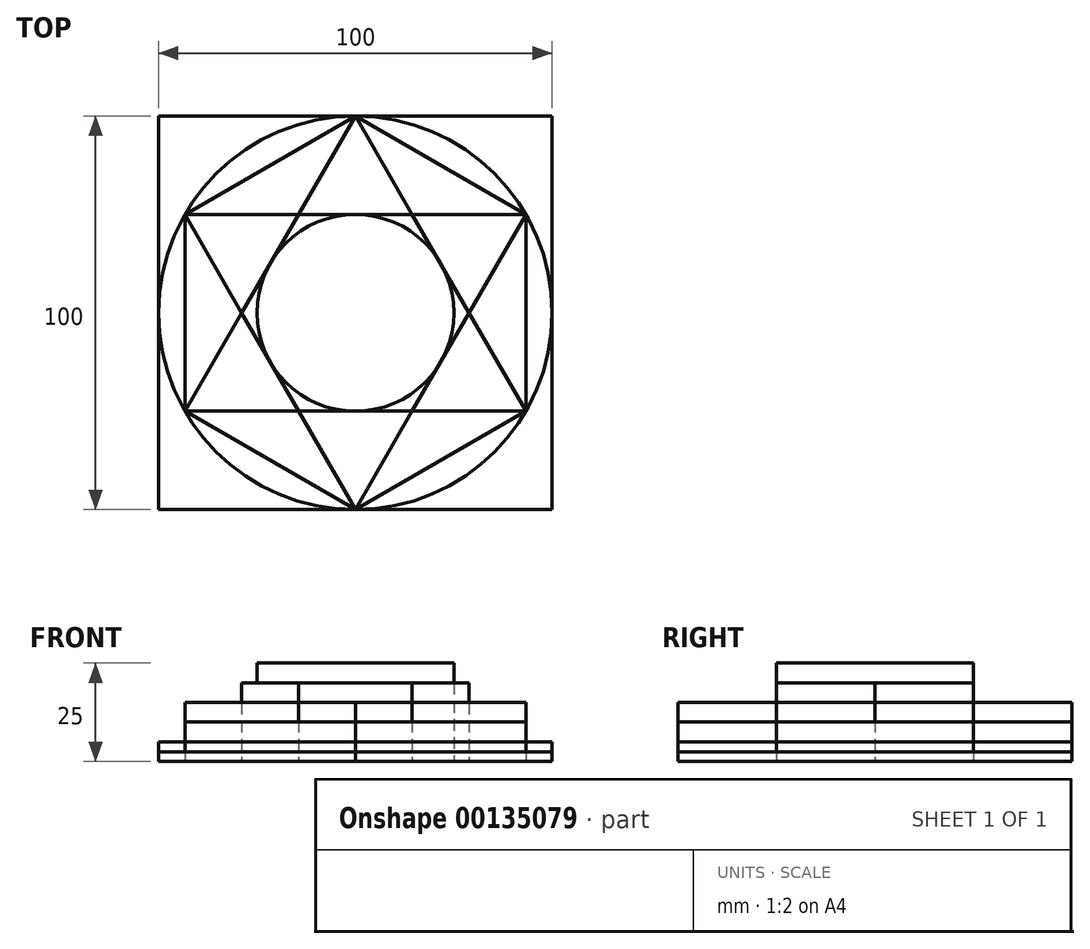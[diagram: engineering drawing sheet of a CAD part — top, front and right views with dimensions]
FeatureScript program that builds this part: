
annotation { "Feature Type Name" : "Feature", "Feature Type Description" : "" }
export const myFeature = defineFeature(function(context is Context, id is Id, definition is map)
    precondition{}
    {
        {
            var Q0;
            Q0=qCreatedBy(makeId("Top.planeOp"),FACE);
            var sketch = newSketch(context, id + "F0", { "sketchPlane" : qUnion([Q0])});
            skCircle(sketch, "E0", {"center": v(0, 0) * mm, "radius": 50 * mm});
            skCircle(sketch, "E1.cCircle", {"center": v(0, 0) * mm, "radius": 50 * mm, "construction": true});
            skLineSegment(sketch, "E1.0", {"start": v(0, 50) * mm, "end": v(43.3, 25) * mm});
            skLineSegment(sketch, "E1.1", {"start": v(43.3, 25) * mm, "end": v(43.3, -25) * mm});
            skLineSegment(sketch, "E1.2", {"start": v(43.3, -25) * mm, "end": v(0, -50) * mm});
            skLineSegment(sketch, "E1.3", {"start": v(0, -50) * mm, "end": v(-43.3, -25) * mm});
            skLineSegment(sketch, "E1.4", {"start": v(-43.3, -25) * mm, "end": v(-43.3, 25) * mm});
            skLineSegment(sketch, "E1.5", {"start": v(-43.3, 25) * mm, "end": v(0, 50) * mm});
            skLineSegment(sketch, "E2", {"start": v(0, 50) * mm, "end": v(-43.3, -25) * mm});
            skLineSegment(sketch, "E3", {"start": v(-43.3, -25) * mm, "end": v(43.3, -25) * mm});
            skLineSegment(sketch, "E4", {"start": v(-43.3, 25) * mm, "end": v(43.3, 25) * mm});
            skLineSegment(sketch, "E5", {"start": v(0, -50) * mm, "end": v(-43.3, 25) * mm});
            skLineSegment(sketch, "E6", {"start": v(0, 50) * mm, "end": v(43.3, -25) * mm});
            skLineSegment(sketch, "E7", {"start": v(43.3, 25) * mm, "end": v(0, -50) * mm});
            skCircle(sketch, "E8", {"center": v(0, 0) * mm, "radius": 25 * mm});
            skLineSegment(sketch, "E9.0", {"start": v(-50, 50) * mm, "end": v(50, 50) * mm});
            skLineSegment(sketch, "E9.1", {"start": v(50, 50) * mm, "end": v(50, -50) * mm});
            skLineSegment(sketch, "E9.2", {"start": v(50, -50) * mm, "end": v(-50, -50) * mm});
            skLineSegment(sketch, "E9.3", {"start": v(-50, -50) * mm, "end": v(-50, 50) * mm});
            skPoint(sketch, "E9.0.midPoint", {"position": v(0, 50) * mm});
            skSolve(sketch);
        }
        {
            var Q0;
            {var subQ0=sQuery(id+"F0.wireOp",EDGE,"E8");var subQ4=makeQuery(id+"F0.imprint","INTERSECT",VERTEX,{"derivedFrom":[sQuery(id+"F0.wireOp",EDGE,"E4"),subQ0]});Q0=makeQuery(id+"F0.imprint","IMPRINT",FACE,{"disambiguationData":[TD([[makeQuery(id+"F0.imprint","IMPRINT",EDGE,{"disambiguationData":[TD([[subQ4,1.0]])],"derivedFrom":subQ0}),1.0]])]});}
            extrude(context, id + "F1", {"entities" : qUnion([Q0]), "depth" : 25 * mm});
        }
        {
            var Q0;
            {var subQ0=sQuery(id+"F0.wireOp",EDGE,"E8");var subQ1=sQuery(id+"F0.wireOp",EDGE,"E2");var subQ2=makeQuery(id+"F0.imprint","INTERSECT",VERTEX,{"derivedFrom":[subQ1,subQ0]});Q0=makeQuery(id+"F0.imprint","IMPRINT",FACE,{"disambiguationData":[TD([[makeQuery(id+"F0.imprint","IMPRINT",EDGE,{"disambiguationData":[TD([[subQ2,-1.0]])],"derivedFrom":subQ1}),1.0]])]});}
            var Q1;
            {var subQ0=sQuery(id+"F0.wireOp",EDGE,"E4");var subQ1=sQuery(id+"F0.wireOp",EDGE,"E2");var subQ2=makeQuery(id+"F0.imprint","INTERSECT",VERTEX,{"derivedFrom":[subQ1,subQ0]});Q1=makeQuery(id+"F0.imprint","IMPRINT",FACE,{"disambiguationData":[TD([[makeQuery(id+"F0.imprint","IMPRINT",EDGE,{"disambiguationData":[TD([[subQ2,-1.0]])],"derivedFrom":subQ1}),1.0]])]});}
            var Q2;
            {var subQ0=sQuery(id+"F0.wireOp",EDGE,"E8");var subQ1=sQuery(id+"F0.wireOp",EDGE,"E4");var subQ2=makeQuery(id+"F0.imprint","INTERSECT",VERTEX,{"derivedFrom":[subQ1,subQ0]});Q2=makeQuery(id+"F0.imprint","IMPRINT",FACE,{"disambiguationData":[TD([[makeQuery(id+"F0.imprint","IMPRINT",EDGE,{"disambiguationData":[TD([[subQ2,-1.0]])],"derivedFrom":subQ1}),-1.0]])]});}
            var Q3;
            {var subQ0=sQuery(id+"F0.wireOp",EDGE,"E8");var subQ1=sQuery(id+"F0.wireOp",EDGE,"E6");var subQ2=makeQuery(id+"F0.imprint","INTERSECT",VERTEX,{"derivedFrom":[subQ1,subQ0]});Q3=makeQuery(id+"F0.imprint","IMPRINT",FACE,{"disambiguationData":[TD([[makeQuery(id+"F0.imprint","IMPRINT",EDGE,{"disambiguationData":[TD([[subQ2,-1.0]])],"derivedFrom":subQ1}),-1.0]])]});}
            var Q4;
            {var subQ0=sQuery(id+"F0.wireOp",EDGE,"E8");var subQ1=sQuery(id+"F0.wireOp",EDGE,"E3");var subQ2=makeQuery(id+"F0.imprint","INTERSECT",VERTEX,{"derivedFrom":[subQ1,subQ0]});Q4=makeQuery(id+"F0.imprint","IMPRINT",FACE,{"disambiguationData":[TD([[makeQuery(id+"F0.imprint","IMPRINT",EDGE,{"disambiguationData":[TD([[subQ2,-1.0]])],"derivedFrom":subQ1}),1.0]])]});}
            var Q5;
            {var subQ0=sQuery(id+"F0.wireOp",EDGE,"E5");var subQ1=sQuery(id+"F0.wireOp",EDGE,"E3");var subQ2=makeQuery(id+"F0.imprint","INTERSECT",VERTEX,{"derivedFrom":[subQ1,subQ0]});Q5=makeQuery(id+"F0.imprint","IMPRINT",FACE,{"disambiguationData":[TD([[makeQuery(id+"F0.imprint","IMPRINT",EDGE,{"disambiguationData":[TD([[subQ2,-1.0]])],"derivedFrom":subQ1}),1.0]])]});}
            var Q6;
            {var subQ0=sQuery(id+"F0.wireOp",EDGE,"E8");var subQ4=makeQuery(id+"F0.imprint","INTERSECT",VERTEX,{"derivedFrom":[sQuery(id+"F0.wireOp",EDGE,"E4"),subQ0]});Q6=makeQuery(id+"F0.imprint","IMPRINT",FACE,{"disambiguationData":[TD([[makeQuery(id+"F0.imprint","IMPRINT",EDGE,{"disambiguationData":[TD([[subQ4,1.0]])],"derivedFrom":subQ0}),1.0]])]});}
            extrude(context, id + "F2", {"entities" : qUnion([Q0, Q1, Q2, Q3, Q4, Q5, Q6]), "depth" : 20 * mm});
        }
        {
            var Q0;
            {var subQ0=sQuery(id+"F0.wireOp",EDGE,"E4");var subQ1=sQuery(id+"F0.wireOp",EDGE,"E2");var subQ2=makeQuery(id+"F0.imprint","INTERSECT",VERTEX,{"derivedFrom":[subQ1,subQ0]});Q0=makeQuery(id+"F0.imprint","IMPRINT",FACE,{"disambiguationData":[TD([[makeQuery(id+"F0.imprint","IMPRINT",EDGE,{"disambiguationData":[TD([[subQ2,-1.0]])],"derivedFrom":subQ1}),1.0]])]});}
            var Q1;
            {var subQ0=sQuery(id+"F0.wireOp",EDGE,"E8");var subQ1=sQuery(id+"F0.wireOp",EDGE,"E4");var subQ2=makeQuery(id+"F0.imprint","INTERSECT",VERTEX,{"derivedFrom":[subQ1,subQ0]});Q1=makeQuery(id+"F0.imprint","IMPRINT",FACE,{"disambiguationData":[TD([[makeQuery(id+"F0.imprint","IMPRINT",EDGE,{"disambiguationData":[TD([[subQ2,-1.0]])],"derivedFrom":subQ1}),-1.0]])]});}
            var Q2;
            {var subQ0=sQuery(id+"F0.wireOp",EDGE,"E8");var subQ4=makeQuery(id+"F0.imprint","INTERSECT",VERTEX,{"derivedFrom":[sQuery(id+"F0.wireOp",EDGE,"E4"),subQ0]});Q2=makeQuery(id+"F0.imprint","IMPRINT",FACE,{"disambiguationData":[TD([[makeQuery(id+"F0.imprint","IMPRINT",EDGE,{"disambiguationData":[TD([[subQ4,1.0]])],"derivedFrom":subQ0}),1.0]])]});}
            var Q3;
            {var subQ0=sQuery(id+"F0.wireOp",EDGE,"E8");var subQ1=sQuery(id+"F0.wireOp",EDGE,"E6");var subQ2=makeQuery(id+"F0.imprint","INTERSECT",VERTEX,{"derivedFrom":[subQ1,subQ0]});Q3=makeQuery(id+"F0.imprint","IMPRINT",FACE,{"disambiguationData":[TD([[makeQuery(id+"F0.imprint","IMPRINT",EDGE,{"disambiguationData":[TD([[subQ2,-1.0]])],"derivedFrom":subQ1}),-1.0]])]});}
            var Q4;
            {var subQ0=sQuery(id+"F0.wireOp",EDGE,"E8");var subQ1=sQuery(id+"F0.wireOp",EDGE,"E3");var subQ2=makeQuery(id+"F0.imprint","INTERSECT",VERTEX,{"derivedFrom":[subQ1,subQ0]});Q4=makeQuery(id+"F0.imprint","IMPRINT",FACE,{"disambiguationData":[TD([[makeQuery(id+"F0.imprint","IMPRINT",EDGE,{"disambiguationData":[TD([[subQ2,-1.0]])],"derivedFrom":subQ1}),1.0]])]});}
            var Q5;
            {var subQ0=sQuery(id+"F0.wireOp",EDGE,"E5");var subQ1=sQuery(id+"F0.wireOp",EDGE,"E3");var subQ2=makeQuery(id+"F0.imprint","INTERSECT",VERTEX,{"derivedFrom":[subQ1,subQ0]});Q5=makeQuery(id+"F0.imprint","IMPRINT",FACE,{"disambiguationData":[TD([[makeQuery(id+"F0.imprint","IMPRINT",EDGE,{"disambiguationData":[TD([[subQ2,-1.0]])],"derivedFrom":subQ1}),1.0]])]});}
            var Q6;
            {var subQ0=sQuery(id+"F0.wireOp",EDGE,"E8");var subQ1=sQuery(id+"F0.wireOp",EDGE,"E2");var subQ2=makeQuery(id+"F0.imprint","INTERSECT",VERTEX,{"derivedFrom":[subQ1,subQ0]});Q6=makeQuery(id+"F0.imprint","IMPRINT",FACE,{"disambiguationData":[TD([[makeQuery(id+"F0.imprint","IMPRINT",EDGE,{"disambiguationData":[TD([[subQ2,-1.0]])],"derivedFrom":subQ1}),1.0]])]});}
            var Q7;
            {var subQ1=sQuery(id+"F0.wireOp",EDGE,"E4");var subQ3=sQuery(id+"F0.wireOp",EDGE,"E6");var subQ4=makeQuery(id+"F0.imprint","INTERSECT",VERTEX,{"derivedFrom":[subQ1,subQ3]});Q7=makeQuery(id+"F0.imprint","IMPRINT",FACE,{"disambiguationData":[TD([[makeQuery(id+"F0.imprint","IMPRINT",EDGE,{"disambiguationData":[TD([[subQ4,-1.0]])],"derivedFrom":subQ3}),1.0]])]});}
            var Q8;
            {var subQ0=sQuery(id+"F0.wireOp",EDGE,"E5");var subQ1=sQuery(id+"F0.wireOp",EDGE,"E3");var subQ2=makeQuery(id+"F0.imprint","INTERSECT",VERTEX,{"derivedFrom":[subQ1,subQ0]});Q8=makeQuery(id+"F0.imprint","IMPRINT",FACE,{"disambiguationData":[TD([[makeQuery(id+"F0.imprint","IMPRINT",EDGE,{"disambiguationData":[TD([[subQ2,-1.0]])],"derivedFrom":subQ1}),-1.0]])]});}
            var Q9;
            {var subQ0=sQuery(id+"F0.wireOp",EDGE,"E6");var subQ3=sQuery(id+"F0.wireOp",EDGE,"E7");var subQ5=makeQuery(id+"F0.imprint","INTERSECT",VERTEX,{"derivedFrom":[subQ0,subQ3]});Q9=makeQuery(id+"F0.imprint","IMPRINT",FACE,{"disambiguationData":[TD([[makeQuery(id+"F0.imprint","IMPRINT",EDGE,{"disambiguationData":[TD([[subQ5,-1.0]])],"derivedFrom":subQ3}),1.0]])]});}
            var Q10;
            {var subQ1=sQuery(id+"F0.wireOp",EDGE,"E2");var subQ3=sQuery(id+"F0.wireOp",EDGE,"E4");var subQ4=makeQuery(id+"F0.imprint","INTERSECT",VERTEX,{"derivedFrom":[subQ1,subQ3]});Q10=makeQuery(id+"F0.imprint","IMPRINT",FACE,{"disambiguationData":[TD([[makeQuery(id+"F0.imprint","IMPRINT",EDGE,{"disambiguationData":[TD([[subQ4,-1.0]])],"derivedFrom":subQ3}),1.0]])]});}
            var Q11;
            {var subQ0=sQuery(id+"F0.wireOp",EDGE,"E4");var subQ1=sQuery(id+"F0.wireOp",EDGE,"E2");var subQ2=makeQuery(id+"F0.imprint","INTERSECT",VERTEX,{"derivedFrom":[subQ1,subQ0]});Q11=makeQuery(id+"F0.imprint","IMPRINT",FACE,{"disambiguationData":[TD([[makeQuery(id+"F0.imprint","IMPRINT",EDGE,{"disambiguationData":[TD([[subQ2,-1.0]])],"derivedFrom":subQ1}),-1.0]])]});}
            var Q12;
            {var subQ0=sQuery(id+"F0.wireOp",EDGE,"E3");var subQ3=sQuery(id+"F0.wireOp",EDGE,"E5");var subQ5=makeQuery(id+"F0.imprint","INTERSECT",VERTEX,{"derivedFrom":[subQ0,subQ3]});Q12=makeQuery(id+"F0.imprint","IMPRINT",FACE,{"disambiguationData":[TD([[makeQuery(id+"F0.imprint","IMPRINT",EDGE,{"disambiguationData":[TD([[subQ5,-1.0]])],"derivedFrom":subQ3}),1.0]])]});}
            extrude(context, id + "F3", {"entities" : qUnion([Q0, Q1, Q2, Q3, Q4, Q5, Q6, Q7, Q8, Q9, Q10, Q11, Q12]), "depth" : 15 * mm});
        }
        {
            var Q0;
            {var subQ0=sQuery(id+"F0.wireOp",EDGE,"E8");var subQ4=makeQuery(id+"F0.imprint","INTERSECT",VERTEX,{"derivedFrom":[sQuery(id+"F0.wireOp",EDGE,"E4"),subQ0]});Q0=makeQuery(id+"F0.imprint","IMPRINT",FACE,{"disambiguationData":[TD([[makeQuery(id+"F0.imprint","IMPRINT",EDGE,{"disambiguationData":[TD([[subQ4,1.0]])],"derivedFrom":subQ0}),1.0]])]});}
            var Q1;
            {var subQ0=sQuery(id+"F0.wireOp",EDGE,"E4");var subQ1=sQuery(id+"F0.wireOp",EDGE,"E2");var subQ2=makeQuery(id+"F0.imprint","INTERSECT",VERTEX,{"derivedFrom":[subQ1,subQ0]});Q1=makeQuery(id+"F0.imprint","IMPRINT",FACE,{"disambiguationData":[TD([[makeQuery(id+"F0.imprint","IMPRINT",EDGE,{"disambiguationData":[TD([[subQ2,-1.0]])],"derivedFrom":subQ1}),1.0]])]});}
            var Q2;
            {var subQ0=sQuery(id+"F0.wireOp",EDGE,"E8");var subQ1=sQuery(id+"F0.wireOp",EDGE,"E4");var subQ2=makeQuery(id+"F0.imprint","INTERSECT",VERTEX,{"derivedFrom":[subQ1,subQ0]});Q2=makeQuery(id+"F0.imprint","IMPRINT",FACE,{"disambiguationData":[TD([[makeQuery(id+"F0.imprint","IMPRINT",EDGE,{"disambiguationData":[TD([[subQ2,-1.0]])],"derivedFrom":subQ1}),-1.0]])]});}
            var Q3;
            {var subQ0=sQuery(id+"F0.wireOp",EDGE,"E8");var subQ1=sQuery(id+"F0.wireOp",EDGE,"E6");var subQ2=makeQuery(id+"F0.imprint","INTERSECT",VERTEX,{"derivedFrom":[subQ1,subQ0]});Q3=makeQuery(id+"F0.imprint","IMPRINT",FACE,{"disambiguationData":[TD([[makeQuery(id+"F0.imprint","IMPRINT",EDGE,{"disambiguationData":[TD([[subQ2,-1.0]])],"derivedFrom":subQ1}),-1.0]])]});}
            var Q4;
            {var subQ0=sQuery(id+"F0.wireOp",EDGE,"E8");var subQ1=sQuery(id+"F0.wireOp",EDGE,"E3");var subQ2=makeQuery(id+"F0.imprint","INTERSECT",VERTEX,{"derivedFrom":[subQ1,subQ0]});Q4=makeQuery(id+"F0.imprint","IMPRINT",FACE,{"disambiguationData":[TD([[makeQuery(id+"F0.imprint","IMPRINT",EDGE,{"disambiguationData":[TD([[subQ2,-1.0]])],"derivedFrom":subQ1}),1.0]])]});}
            var Q5;
            {var subQ0=sQuery(id+"F0.wireOp",EDGE,"E5");var subQ1=sQuery(id+"F0.wireOp",EDGE,"E3");var subQ2=makeQuery(id+"F0.imprint","INTERSECT",VERTEX,{"derivedFrom":[subQ1,subQ0]});Q5=makeQuery(id+"F0.imprint","IMPRINT",FACE,{"disambiguationData":[TD([[makeQuery(id+"F0.imprint","IMPRINT",EDGE,{"disambiguationData":[TD([[subQ2,-1.0]])],"derivedFrom":subQ1}),1.0]])]});}
            var Q6;
            {var subQ0=sQuery(id+"F0.wireOp",EDGE,"E8");var subQ1=sQuery(id+"F0.wireOp",EDGE,"E2");var subQ2=makeQuery(id+"F0.imprint","INTERSECT",VERTEX,{"derivedFrom":[subQ1,subQ0]});Q6=makeQuery(id+"F0.imprint","IMPRINT",FACE,{"disambiguationData":[TD([[makeQuery(id+"F0.imprint","IMPRINT",EDGE,{"disambiguationData":[TD([[subQ2,-1.0]])],"derivedFrom":subQ1}),1.0]])]});}
            var Q7;
            {var subQ0=sQuery(id+"F0.wireOp",EDGE,"E4");var subQ1=sQuery(id+"F0.wireOp",EDGE,"E2");var subQ2=makeQuery(id+"F0.imprint","INTERSECT",VERTEX,{"derivedFrom":[subQ1,subQ0]});Q7=makeQuery(id+"F0.imprint","IMPRINT",FACE,{"disambiguationData":[TD([[makeQuery(id+"F0.imprint","IMPRINT",EDGE,{"disambiguationData":[TD([[subQ2,-1.0]])],"derivedFrom":subQ1}),-1.0]])]});}
            var Q8;
            {var subQ0=sQuery(id+"F0.wireOp",EDGE,"E3");var subQ3=sQuery(id+"F0.wireOp",EDGE,"E5");var subQ5=makeQuery(id+"F0.imprint","INTERSECT",VERTEX,{"derivedFrom":[subQ0,subQ3]});Q8=makeQuery(id+"F0.imprint","IMPRINT",FACE,{"disambiguationData":[TD([[makeQuery(id+"F0.imprint","IMPRINT",EDGE,{"disambiguationData":[TD([[subQ5,-1.0]])],"derivedFrom":subQ3}),1.0]])]});}
            var Q9;
            {var subQ0=sQuery(id+"F0.wireOp",EDGE,"E5");var subQ1=sQuery(id+"F0.wireOp",EDGE,"E3");var subQ2=makeQuery(id+"F0.imprint","INTERSECT",VERTEX,{"derivedFrom":[subQ1,subQ0]});Q9=makeQuery(id+"F0.imprint","IMPRINT",FACE,{"disambiguationData":[TD([[makeQuery(id+"F0.imprint","IMPRINT",EDGE,{"disambiguationData":[TD([[subQ2,-1.0]])],"derivedFrom":subQ1}),-1.0]])]});}
            var Q10;
            {var subQ0=sQuery(id+"F0.wireOp",EDGE,"E6");var subQ3=sQuery(id+"F0.wireOp",EDGE,"E7");var subQ5=makeQuery(id+"F0.imprint","INTERSECT",VERTEX,{"derivedFrom":[subQ0,subQ3]});Q10=makeQuery(id+"F0.imprint","IMPRINT",FACE,{"disambiguationData":[TD([[makeQuery(id+"F0.imprint","IMPRINT",EDGE,{"disambiguationData":[TD([[subQ5,-1.0]])],"derivedFrom":subQ3}),1.0]])]});}
            var Q11;
            {var subQ1=sQuery(id+"F0.wireOp",EDGE,"E4");var subQ3=sQuery(id+"F0.wireOp",EDGE,"E6");var subQ4=makeQuery(id+"F0.imprint","INTERSECT",VERTEX,{"derivedFrom":[subQ1,subQ3]});Q11=makeQuery(id+"F0.imprint","IMPRINT",FACE,{"disambiguationData":[TD([[makeQuery(id+"F0.imprint","IMPRINT",EDGE,{"disambiguationData":[TD([[subQ4,-1.0]])],"derivedFrom":subQ3}),1.0]])]});}
            var Q12;
            {var subQ1=sQuery(id+"F0.wireOp",EDGE,"E2");var subQ3=sQuery(id+"F0.wireOp",EDGE,"E4");var subQ4=makeQuery(id+"F0.imprint","INTERSECT",VERTEX,{"derivedFrom":[subQ1,subQ3]});Q12=makeQuery(id+"F0.imprint","IMPRINT",FACE,{"disambiguationData":[TD([[makeQuery(id+"F0.imprint","IMPRINT",EDGE,{"disambiguationData":[TD([[subQ4,-1.0]])],"derivedFrom":subQ3}),1.0]])]});}
            var Q13;
            {var subQ0=sQuery(id+"F0.wireOp",EDGE,"E1.5");Q13=makeQuery(id+"F0.imprint","IMPRINT",FACE,{"disambiguationData":[TD([[makeQuery(id+"F0.imprint","IMPRINT",EDGE,{"derivedFrom":subQ0}),-1.0]])]});}
            var Q14;
            {var subQ0=sQuery(id+"F0.wireOp",EDGE,"E1.0");Q14=makeQuery(id+"F0.imprint","IMPRINT",FACE,{"disambiguationData":[TD([[makeQuery(id+"F0.imprint","IMPRINT",EDGE,{"derivedFrom":subQ0}),-1.0]])]});}
            var Q15;
            {var subQ0=sQuery(id+"F0.wireOp",EDGE,"E1.1");Q15=makeQuery(id+"F0.imprint","IMPRINT",FACE,{"disambiguationData":[TD([[makeQuery(id+"F0.imprint","IMPRINT",EDGE,{"derivedFrom":subQ0}),-1.0]])]});}
            var Q16;
            {var subQ0=sQuery(id+"F0.wireOp",EDGE,"E1.2");Q16=makeQuery(id+"F0.imprint","IMPRINT",FACE,{"disambiguationData":[TD([[makeQuery(id+"F0.imprint","IMPRINT",EDGE,{"derivedFrom":subQ0}),-1.0]])]});}
            var Q17;
            {var subQ0=sQuery(id+"F0.wireOp",EDGE,"E1.3");Q17=makeQuery(id+"F0.imprint","IMPRINT",FACE,{"disambiguationData":[TD([[makeQuery(id+"F0.imprint","IMPRINT",EDGE,{"derivedFrom":subQ0}),-1.0]])]});}
            var Q18;
            {var subQ0=sQuery(id+"F0.wireOp",EDGE,"E1.4");Q18=makeQuery(id+"F0.imprint","IMPRINT",FACE,{"disambiguationData":[TD([[makeQuery(id+"F0.imprint","IMPRINT",EDGE,{"derivedFrom":subQ0}),-1.0]])]});}
            extrude(context, id + "F4", {"entities" : qUnion([Q0, Q1, Q2, Q3, Q4, Q5, Q6, Q7, Q8, Q9, Q10, Q11, Q12, Q13, Q14, Q15, Q16, Q17, Q18]), "depth" : 10 * mm});
        }
        {
            var Q0;
            {var subQ0=sQuery(id+"F0.wireOp",EDGE,"E1.5");Q0=makeQuery(id+"F0.imprint","IMPRINT",FACE,{"disambiguationData":[TD([[makeQuery(id+"F0.imprint","IMPRINT",EDGE,{"derivedFrom":subQ0}),1.0]])]});}
            var Q1;
            {var subQ0=sQuery(id+"F0.wireOp",EDGE,"E1.0");Q1=makeQuery(id+"F0.imprint","IMPRINT",FACE,{"disambiguationData":[TD([[makeQuery(id+"F0.imprint","IMPRINT",EDGE,{"derivedFrom":subQ0}),1.0]])]});}
            var Q2;
            {var subQ0=sQuery(id+"F0.wireOp",EDGE,"E1.5");Q2=makeQuery(id+"F0.imprint","IMPRINT",FACE,{"disambiguationData":[TD([[makeQuery(id+"F0.imprint","IMPRINT",EDGE,{"derivedFrom":subQ0}),-1.0]])]});}
            var Q3;
            {var subQ1=sQuery(id+"F0.wireOp",EDGE,"E2");var subQ3=sQuery(id+"F0.wireOp",EDGE,"E4");var subQ4=makeQuery(id+"F0.imprint","INTERSECT",VERTEX,{"derivedFrom":[subQ1,subQ3]});Q3=makeQuery(id+"F0.imprint","IMPRINT",FACE,{"disambiguationData":[TD([[makeQuery(id+"F0.imprint","IMPRINT",EDGE,{"disambiguationData":[TD([[subQ4,-1.0]])],"derivedFrom":subQ3}),1.0]])]});}
            var Q4;
            {var subQ0=sQuery(id+"F0.wireOp",EDGE,"E1.0");Q4=makeQuery(id+"F0.imprint","IMPRINT",FACE,{"disambiguationData":[TD([[makeQuery(id+"F0.imprint","IMPRINT",EDGE,{"derivedFrom":subQ0}),-1.0]])]});}
            var Q5;
            {var subQ0=sQuery(id+"F0.wireOp",EDGE,"E4");var subQ1=sQuery(id+"F0.wireOp",EDGE,"E2");var subQ2=makeQuery(id+"F0.imprint","INTERSECT",VERTEX,{"derivedFrom":[subQ1,subQ0]});Q5=makeQuery(id+"F0.imprint","IMPRINT",FACE,{"disambiguationData":[TD([[makeQuery(id+"F0.imprint","IMPRINT",EDGE,{"disambiguationData":[TD([[subQ2,-1.0]])],"derivedFrom":subQ1}),-1.0]])]});}
            var Q6;
            {var subQ0=sQuery(id+"F0.wireOp",EDGE,"E4");var subQ1=sQuery(id+"F0.wireOp",EDGE,"E2");var subQ2=makeQuery(id+"F0.imprint","INTERSECT",VERTEX,{"derivedFrom":[subQ1,subQ0]});Q6=makeQuery(id+"F0.imprint","IMPRINT",FACE,{"disambiguationData":[TD([[makeQuery(id+"F0.imprint","IMPRINT",EDGE,{"disambiguationData":[TD([[subQ2,-1.0]])],"derivedFrom":subQ1}),1.0]])]});}
            var Q7;
            {var subQ0=sQuery(id+"F0.wireOp",EDGE,"E8");var subQ1=sQuery(id+"F0.wireOp",EDGE,"E4");var subQ2=makeQuery(id+"F0.imprint","INTERSECT",VERTEX,{"derivedFrom":[subQ1,subQ0]});Q7=makeQuery(id+"F0.imprint","IMPRINT",FACE,{"disambiguationData":[TD([[makeQuery(id+"F0.imprint","IMPRINT",EDGE,{"disambiguationData":[TD([[subQ2,-1.0]])],"derivedFrom":subQ1}),-1.0]])]});}
            var Q8;
            {var subQ1=sQuery(id+"F0.wireOp",EDGE,"E4");var subQ3=sQuery(id+"F0.wireOp",EDGE,"E6");var subQ4=makeQuery(id+"F0.imprint","INTERSECT",VERTEX,{"derivedFrom":[subQ1,subQ3]});Q8=makeQuery(id+"F0.imprint","IMPRINT",FACE,{"disambiguationData":[TD([[makeQuery(id+"F0.imprint","IMPRINT",EDGE,{"disambiguationData":[TD([[subQ4,-1.0]])],"derivedFrom":subQ3}),1.0]])]});}
            var Q9;
            {var subQ0=sQuery(id+"F0.wireOp",EDGE,"E1.1");Q9=makeQuery(id+"F0.imprint","IMPRINT",FACE,{"disambiguationData":[TD([[makeQuery(id+"F0.imprint","IMPRINT",EDGE,{"derivedFrom":subQ0}),1.0]])]});}
            var Q10;
            {var subQ0=sQuery(id+"F0.wireOp",EDGE,"E1.1");Q10=makeQuery(id+"F0.imprint","IMPRINT",FACE,{"disambiguationData":[TD([[makeQuery(id+"F0.imprint","IMPRINT",EDGE,{"derivedFrom":subQ0}),-1.0]])]});}
            var Q11;
            {var subQ0=sQuery(id+"F0.wireOp",EDGE,"E8");var subQ1=sQuery(id+"F0.wireOp",EDGE,"E6");var subQ2=makeQuery(id+"F0.imprint","INTERSECT",VERTEX,{"derivedFrom":[subQ1,subQ0]});Q11=makeQuery(id+"F0.imprint","IMPRINT",FACE,{"disambiguationData":[TD([[makeQuery(id+"F0.imprint","IMPRINT",EDGE,{"disambiguationData":[TD([[subQ2,-1.0]])],"derivedFrom":subQ1}),-1.0]])]});}
            var Q12;
            {var subQ0=sQuery(id+"F0.wireOp",EDGE,"E8");var subQ4=makeQuery(id+"F0.imprint","INTERSECT",VERTEX,{"derivedFrom":[sQuery(id+"F0.wireOp",EDGE,"E4"),subQ0]});Q12=makeQuery(id+"F0.imprint","IMPRINT",FACE,{"disambiguationData":[TD([[makeQuery(id+"F0.imprint","IMPRINT",EDGE,{"disambiguationData":[TD([[subQ4,1.0]])],"derivedFrom":subQ0}),1.0]])]});}
            var Q13;
            {var subQ0=sQuery(id+"F0.wireOp",EDGE,"E8");var subQ1=sQuery(id+"F0.wireOp",EDGE,"E2");var subQ2=makeQuery(id+"F0.imprint","INTERSECT",VERTEX,{"derivedFrom":[subQ1,subQ0]});Q13=makeQuery(id+"F0.imprint","IMPRINT",FACE,{"disambiguationData":[TD([[makeQuery(id+"F0.imprint","IMPRINT",EDGE,{"disambiguationData":[TD([[subQ2,-1.0]])],"derivedFrom":subQ1}),1.0]])]});}
            var Q14;
            {var subQ0=sQuery(id+"F0.wireOp",EDGE,"E1.4");Q14=makeQuery(id+"F0.imprint","IMPRINT",FACE,{"disambiguationData":[TD([[makeQuery(id+"F0.imprint","IMPRINT",EDGE,{"derivedFrom":subQ0}),-1.0]])]});}
            var Q15;
            {var subQ0=sQuery(id+"F0.wireOp",EDGE,"E1.4");Q15=makeQuery(id+"F0.imprint","IMPRINT",FACE,{"disambiguationData":[TD([[makeQuery(id+"F0.imprint","IMPRINT",EDGE,{"derivedFrom":subQ0}),1.0]])]});}
            var Q16;
            {var subQ0=sQuery(id+"F0.wireOp",EDGE,"E3");var subQ3=sQuery(id+"F0.wireOp",EDGE,"E5");var subQ5=makeQuery(id+"F0.imprint","INTERSECT",VERTEX,{"derivedFrom":[subQ0,subQ3]});Q16=makeQuery(id+"F0.imprint","IMPRINT",FACE,{"disambiguationData":[TD([[makeQuery(id+"F0.imprint","IMPRINT",EDGE,{"disambiguationData":[TD([[subQ5,-1.0]])],"derivedFrom":subQ3}),1.0]])]});}
            var Q17;
            {var subQ0=sQuery(id+"F0.wireOp",EDGE,"E5");var subQ1=sQuery(id+"F0.wireOp",EDGE,"E3");var subQ2=makeQuery(id+"F0.imprint","INTERSECT",VERTEX,{"derivedFrom":[subQ1,subQ0]});Q17=makeQuery(id+"F0.imprint","IMPRINT",FACE,{"disambiguationData":[TD([[makeQuery(id+"F0.imprint","IMPRINT",EDGE,{"disambiguationData":[TD([[subQ2,-1.0]])],"derivedFrom":subQ1}),1.0]])]});}
            var Q18;
            {var subQ0=sQuery(id+"F0.wireOp",EDGE,"E8");var subQ1=sQuery(id+"F0.wireOp",EDGE,"E3");var subQ2=makeQuery(id+"F0.imprint","INTERSECT",VERTEX,{"derivedFrom":[subQ1,subQ0]});Q18=makeQuery(id+"F0.imprint","IMPRINT",FACE,{"disambiguationData":[TD([[makeQuery(id+"F0.imprint","IMPRINT",EDGE,{"disambiguationData":[TD([[subQ2,-1.0]])],"derivedFrom":subQ1}),1.0]])]});}
            var Q19;
            {var subQ0=sQuery(id+"F0.wireOp",EDGE,"E6");var subQ3=sQuery(id+"F0.wireOp",EDGE,"E7");var subQ5=makeQuery(id+"F0.imprint","INTERSECT",VERTEX,{"derivedFrom":[subQ0,subQ3]});Q19=makeQuery(id+"F0.imprint","IMPRINT",FACE,{"disambiguationData":[TD([[makeQuery(id+"F0.imprint","IMPRINT",EDGE,{"disambiguationData":[TD([[subQ5,-1.0]])],"derivedFrom":subQ3}),1.0]])]});}
            var Q20;
            {var subQ0=sQuery(id+"F0.wireOp",EDGE,"E1.2");Q20=makeQuery(id+"F0.imprint","IMPRINT",FACE,{"disambiguationData":[TD([[makeQuery(id+"F0.imprint","IMPRINT",EDGE,{"derivedFrom":subQ0}),-1.0]])]});}
            var Q21;
            {var subQ0=sQuery(id+"F0.wireOp",EDGE,"E5");var subQ1=sQuery(id+"F0.wireOp",EDGE,"E3");var subQ2=makeQuery(id+"F0.imprint","INTERSECT",VERTEX,{"derivedFrom":[subQ1,subQ0]});Q21=makeQuery(id+"F0.imprint","IMPRINT",FACE,{"disambiguationData":[TD([[makeQuery(id+"F0.imprint","IMPRINT",EDGE,{"disambiguationData":[TD([[subQ2,-1.0]])],"derivedFrom":subQ1}),-1.0]])]});}
            var Q22;
            {var subQ0=sQuery(id+"F0.wireOp",EDGE,"E1.3");Q22=makeQuery(id+"F0.imprint","IMPRINT",FACE,{"disambiguationData":[TD([[makeQuery(id+"F0.imprint","IMPRINT",EDGE,{"derivedFrom":subQ0}),-1.0]])]});}
            var Q23;
            {var subQ0=sQuery(id+"F0.wireOp",EDGE,"E1.3");Q23=makeQuery(id+"F0.imprint","IMPRINT",FACE,{"disambiguationData":[TD([[makeQuery(id+"F0.imprint","IMPRINT",EDGE,{"derivedFrom":subQ0}),1.0]])]});}
            var Q24;
            {var subQ0=sQuery(id+"F0.wireOp",EDGE,"E1.2");Q24=makeQuery(id+"F0.imprint","IMPRINT",FACE,{"disambiguationData":[TD([[makeQuery(id+"F0.imprint","IMPRINT",EDGE,{"derivedFrom":subQ0}),1.0]])]});}
            extrude(context, id + "F5", {"entities" : qUnion([Q0, Q1, Q2, Q3, Q4, Q5, Q6, Q7, Q8, Q9, Q10, Q11, Q12, Q13, Q14, Q15, Q16, Q17, Q18, Q19, Q20, Q21, Q22, Q23, Q24]), "depth" : 5 * mm});
        }
        {
            var Q0;
            {var subQ0=sQuery(id+"F0.wireOp",EDGE,"E9.0");var subQ5=sQuery(id+"F0.wireOp",EDGE,"E9.3");var subQ7=makeQuery(id+"F0.imprint","INTERSECT",VERTEX,{"derivedFrom":[subQ0,subQ5]});Q0=makeQuery(id+"F0.imprint","IMPRINT",FACE,{"disambiguationData":[TD([[makeQuery(id+"F0.imprint","IMPRINT",EDGE,{"disambiguationData":[TD([[subQ7,1.0]])],"derivedFrom":subQ5}),-1.0]])]});}
            var Q1;
            {var subQ0=sQuery(id+"F0.wireOp",EDGE,"E1.5");Q1=makeQuery(id+"F0.imprint","IMPRINT",FACE,{"disambiguationData":[TD([[makeQuery(id+"F0.imprint","IMPRINT",EDGE,{"derivedFrom":subQ0}),1.0]])]});}
            var Q2;
            {var subQ0=sQuery(id+"F0.wireOp",EDGE,"E1.5");Q2=makeQuery(id+"F0.imprint","IMPRINT",FACE,{"disambiguationData":[TD([[makeQuery(id+"F0.imprint","IMPRINT",EDGE,{"derivedFrom":subQ0}),-1.0]])]});}
            var Q3;
            {var subQ1=sQuery(id+"F0.wireOp",EDGE,"E2");var subQ3=sQuery(id+"F0.wireOp",EDGE,"E4");var subQ4=makeQuery(id+"F0.imprint","INTERSECT",VERTEX,{"derivedFrom":[subQ1,subQ3]});Q3=makeQuery(id+"F0.imprint","IMPRINT",FACE,{"disambiguationData":[TD([[makeQuery(id+"F0.imprint","IMPRINT",EDGE,{"disambiguationData":[TD([[subQ4,-1.0]])],"derivedFrom":subQ3}),1.0]])]});}
            var Q4;
            {var subQ0=sQuery(id+"F0.wireOp",EDGE,"E1.0");Q4=makeQuery(id+"F0.imprint","IMPRINT",FACE,{"disambiguationData":[TD([[makeQuery(id+"F0.imprint","IMPRINT",EDGE,{"derivedFrom":subQ0}),1.0]])]});}
            var Q5;
            {var subQ0=sQuery(id+"F0.wireOp",EDGE,"E1.0");Q5=makeQuery(id+"F0.imprint","IMPRINT",FACE,{"disambiguationData":[TD([[makeQuery(id+"F0.imprint","IMPRINT",EDGE,{"derivedFrom":subQ0}),-1.0]])]});}
            var Q6;
            {var subQ3=sQuery(id+"F0.wireOp",EDGE,"E9.1");var subQ5=sQuery(id+"F0.wireOp",EDGE,"E9.0");var subQ7=makeQuery(id+"F0.imprint","INTERSECT",VERTEX,{"derivedFrom":[subQ5,subQ3]});Q6=makeQuery(id+"F0.imprint","IMPRINT",FACE,{"disambiguationData":[TD([[makeQuery(id+"F0.imprint","IMPRINT",EDGE,{"disambiguationData":[TD([[subQ7,-1.0]])],"derivedFrom":subQ3}),-1.0]])]});}
            var Q7;
            {var subQ1=sQuery(id+"F0.wireOp",EDGE,"E4");var subQ3=sQuery(id+"F0.wireOp",EDGE,"E6");var subQ4=makeQuery(id+"F0.imprint","INTERSECT",VERTEX,{"derivedFrom":[subQ1,subQ3]});Q7=makeQuery(id+"F0.imprint","IMPRINT",FACE,{"disambiguationData":[TD([[makeQuery(id+"F0.imprint","IMPRINT",EDGE,{"disambiguationData":[TD([[subQ4,-1.0]])],"derivedFrom":subQ3}),1.0]])]});}
            var Q8;
            {var subQ0=sQuery(id+"F0.wireOp",EDGE,"E1.1");Q8=makeQuery(id+"F0.imprint","IMPRINT",FACE,{"disambiguationData":[TD([[makeQuery(id+"F0.imprint","IMPRINT",EDGE,{"derivedFrom":subQ0}),-1.0]])]});}
            var Q9;
            {var subQ0=sQuery(id+"F0.wireOp",EDGE,"E1.1");Q9=makeQuery(id+"F0.imprint","IMPRINT",FACE,{"disambiguationData":[TD([[makeQuery(id+"F0.imprint","IMPRINT",EDGE,{"derivedFrom":subQ0}),1.0]])]});}
            var Q10;
            {var subQ0=sQuery(id+"F0.wireOp",EDGE,"E8");var subQ4=makeQuery(id+"F0.imprint","INTERSECT",VERTEX,{"derivedFrom":[sQuery(id+"F0.wireOp",EDGE,"E4"),subQ0]});Q10=makeQuery(id+"F0.imprint","IMPRINT",FACE,{"disambiguationData":[TD([[makeQuery(id+"F0.imprint","IMPRINT",EDGE,{"disambiguationData":[TD([[subQ4,1.0]])],"derivedFrom":subQ0}),1.0]])]});}
            var Q11;
            {var subQ0=sQuery(id+"F0.wireOp",EDGE,"E4");var subQ1=sQuery(id+"F0.wireOp",EDGE,"E2");var subQ2=makeQuery(id+"F0.imprint","INTERSECT",VERTEX,{"derivedFrom":[subQ1,subQ0]});Q11=makeQuery(id+"F0.imprint","IMPRINT",FACE,{"disambiguationData":[TD([[makeQuery(id+"F0.imprint","IMPRINT",EDGE,{"disambiguationData":[TD([[subQ2,-1.0]])],"derivedFrom":subQ1}),-1.0]])]});}
            var Q12;
            {var subQ0=sQuery(id+"F0.wireOp",EDGE,"E1.4");Q12=makeQuery(id+"F0.imprint","IMPRINT",FACE,{"disambiguationData":[TD([[makeQuery(id+"F0.imprint","IMPRINT",EDGE,{"derivedFrom":subQ0}),-1.0]])]});}
            var Q13;
            {var subQ0=sQuery(id+"F0.wireOp",EDGE,"E1.4");Q13=makeQuery(id+"F0.imprint","IMPRINT",FACE,{"disambiguationData":[TD([[makeQuery(id+"F0.imprint","IMPRINT",EDGE,{"derivedFrom":subQ0}),1.0]])]});}
            var Q14;
            {var subQ0=sQuery(id+"F0.wireOp",EDGE,"E3");var subQ3=sQuery(id+"F0.wireOp",EDGE,"E5");var subQ5=makeQuery(id+"F0.imprint","INTERSECT",VERTEX,{"derivedFrom":[subQ0,subQ3]});Q14=makeQuery(id+"F0.imprint","IMPRINT",FACE,{"disambiguationData":[TD([[makeQuery(id+"F0.imprint","IMPRINT",EDGE,{"disambiguationData":[TD([[subQ5,-1.0]])],"derivedFrom":subQ3}),1.0]])]});}
            var Q15;
            {var subQ3=sQuery(id+"F0.wireOp",EDGE,"E9.3");var subQ5=sQuery(id+"F0.wireOp",EDGE,"E9.2");var subQ7=makeQuery(id+"F0.imprint","INTERSECT",VERTEX,{"derivedFrom":[subQ5,subQ3]});Q15=makeQuery(id+"F0.imprint","IMPRINT",FACE,{"disambiguationData":[TD([[makeQuery(id+"F0.imprint","IMPRINT",EDGE,{"disambiguationData":[TD([[subQ7,-1.0]])],"derivedFrom":subQ3}),-1.0]])]});}
            var Q16;
            {var subQ0=sQuery(id+"F0.wireOp",EDGE,"E1.3");Q16=makeQuery(id+"F0.imprint","IMPRINT",FACE,{"disambiguationData":[TD([[makeQuery(id+"F0.imprint","IMPRINT",EDGE,{"derivedFrom":subQ0}),1.0]])]});}
            var Q17;
            {var subQ0=sQuery(id+"F0.wireOp",EDGE,"E1.3");Q17=makeQuery(id+"F0.imprint","IMPRINT",FACE,{"disambiguationData":[TD([[makeQuery(id+"F0.imprint","IMPRINT",EDGE,{"derivedFrom":subQ0}),-1.0]])]});}
            var Q18;
            {var subQ0=sQuery(id+"F0.wireOp",EDGE,"E5");var subQ1=sQuery(id+"F0.wireOp",EDGE,"E3");var subQ2=makeQuery(id+"F0.imprint","INTERSECT",VERTEX,{"derivedFrom":[subQ1,subQ0]});Q18=makeQuery(id+"F0.imprint","IMPRINT",FACE,{"disambiguationData":[TD([[makeQuery(id+"F0.imprint","IMPRINT",EDGE,{"disambiguationData":[TD([[subQ2,-1.0]])],"derivedFrom":subQ1}),-1.0]])]});}
            var Q19;
            {var subQ0=sQuery(id+"F0.wireOp",EDGE,"E1.2");Q19=makeQuery(id+"F0.imprint","IMPRINT",FACE,{"disambiguationData":[TD([[makeQuery(id+"F0.imprint","IMPRINT",EDGE,{"derivedFrom":subQ0}),-1.0]])]});}
            var Q20;
            {var subQ0=sQuery(id+"F0.wireOp",EDGE,"E6");var subQ3=sQuery(id+"F0.wireOp",EDGE,"E7");var subQ5=makeQuery(id+"F0.imprint","INTERSECT",VERTEX,{"derivedFrom":[subQ0,subQ3]});Q20=makeQuery(id+"F0.imprint","IMPRINT",FACE,{"disambiguationData":[TD([[makeQuery(id+"F0.imprint","IMPRINT",EDGE,{"disambiguationData":[TD([[subQ5,-1.0]])],"derivedFrom":subQ3}),1.0]])]});}
            var Q21;
            {var subQ0=sQuery(id+"F0.wireOp",EDGE,"E1.2");Q21=makeQuery(id+"F0.imprint","IMPRINT",FACE,{"disambiguationData":[TD([[makeQuery(id+"F0.imprint","IMPRINT",EDGE,{"derivedFrom":subQ0}),1.0]])]});}
            var Q22;
            {var subQ3=sQuery(id+"F0.wireOp",EDGE,"E9.2");var subQ5=sQuery(id+"F0.wireOp",EDGE,"E9.1");var subQ7=makeQuery(id+"F0.imprint","INTERSECT",VERTEX,{"derivedFrom":[subQ5,subQ3]});Q22=makeQuery(id+"F0.imprint","IMPRINT",FACE,{"disambiguationData":[TD([[makeQuery(id+"F0.imprint","IMPRINT",EDGE,{"disambiguationData":[TD([[subQ7,1.0]])],"derivedFrom":subQ5}),-1.0]])]});}
            var Q23;
            {var subQ0=sQuery(id+"F0.wireOp",EDGE,"E4");var subQ1=sQuery(id+"F0.wireOp",EDGE,"E2");var subQ2=makeQuery(id+"F0.imprint","INTERSECT",VERTEX,{"derivedFrom":[subQ1,subQ0]});Q23=makeQuery(id+"F0.imprint","IMPRINT",FACE,{"disambiguationData":[TD([[makeQuery(id+"F0.imprint","IMPRINT",EDGE,{"disambiguationData":[TD([[subQ2,-1.0]])],"derivedFrom":subQ1}),1.0]])]});}
            var Q24;
            {var subQ0=sQuery(id+"F0.wireOp",EDGE,"E8");var subQ1=sQuery(id+"F0.wireOp",EDGE,"E4");var subQ2=makeQuery(id+"F0.imprint","INTERSECT",VERTEX,{"derivedFrom":[subQ1,subQ0]});Q24=makeQuery(id+"F0.imprint","IMPRINT",FACE,{"disambiguationData":[TD([[makeQuery(id+"F0.imprint","IMPRINT",EDGE,{"disambiguationData":[TD([[subQ2,-1.0]])],"derivedFrom":subQ1}),-1.0]])]});}
            var Q25;
            {var subQ0=sQuery(id+"F0.wireOp",EDGE,"E8");var subQ1=sQuery(id+"F0.wireOp",EDGE,"E2");var subQ2=makeQuery(id+"F0.imprint","INTERSECT",VERTEX,{"derivedFrom":[subQ1,subQ0]});Q25=makeQuery(id+"F0.imprint","IMPRINT",FACE,{"disambiguationData":[TD([[makeQuery(id+"F0.imprint","IMPRINT",EDGE,{"disambiguationData":[TD([[subQ2,-1.0]])],"derivedFrom":subQ1}),1.0]])]});}
            var Q26;
            {var subQ0=sQuery(id+"F0.wireOp",EDGE,"E5");var subQ1=sQuery(id+"F0.wireOp",EDGE,"E3");var subQ2=makeQuery(id+"F0.imprint","INTERSECT",VERTEX,{"derivedFrom":[subQ1,subQ0]});Q26=makeQuery(id+"F0.imprint","IMPRINT",FACE,{"disambiguationData":[TD([[makeQuery(id+"F0.imprint","IMPRINT",EDGE,{"disambiguationData":[TD([[subQ2,-1.0]])],"derivedFrom":subQ1}),1.0]])]});}
            var Q27;
            {var subQ0=sQuery(id+"F0.wireOp",EDGE,"E8");var subQ1=sQuery(id+"F0.wireOp",EDGE,"E3");var subQ2=makeQuery(id+"F0.imprint","INTERSECT",VERTEX,{"derivedFrom":[subQ1,subQ0]});Q27=makeQuery(id+"F0.imprint","IMPRINT",FACE,{"disambiguationData":[TD([[makeQuery(id+"F0.imprint","IMPRINT",EDGE,{"disambiguationData":[TD([[subQ2,-1.0]])],"derivedFrom":subQ1}),1.0]])]});}
            var Q28;
            {var subQ0=sQuery(id+"F0.wireOp",EDGE,"E8");var subQ1=sQuery(id+"F0.wireOp",EDGE,"E6");var subQ2=makeQuery(id+"F0.imprint","INTERSECT",VERTEX,{"derivedFrom":[subQ1,subQ0]});Q28=makeQuery(id+"F0.imprint","IMPRINT",FACE,{"disambiguationData":[TD([[makeQuery(id+"F0.imprint","IMPRINT",EDGE,{"disambiguationData":[TD([[subQ2,-1.0]])],"derivedFrom":subQ1}),-1.0]])]});}
            extrude(context, id + "F6", {"entities" : qUnion([Q0, Q1, Q2, Q3, Q4, Q5, Q6, Q7, Q8, Q9, Q10, Q11, Q12, Q13, Q14, Q15, Q16, Q17, Q18, Q19, Q20, Q21, Q22, Q23, Q24, Q25, Q26, Q27, Q28]), "depth" : 2.5 * mm});
        }
    });
